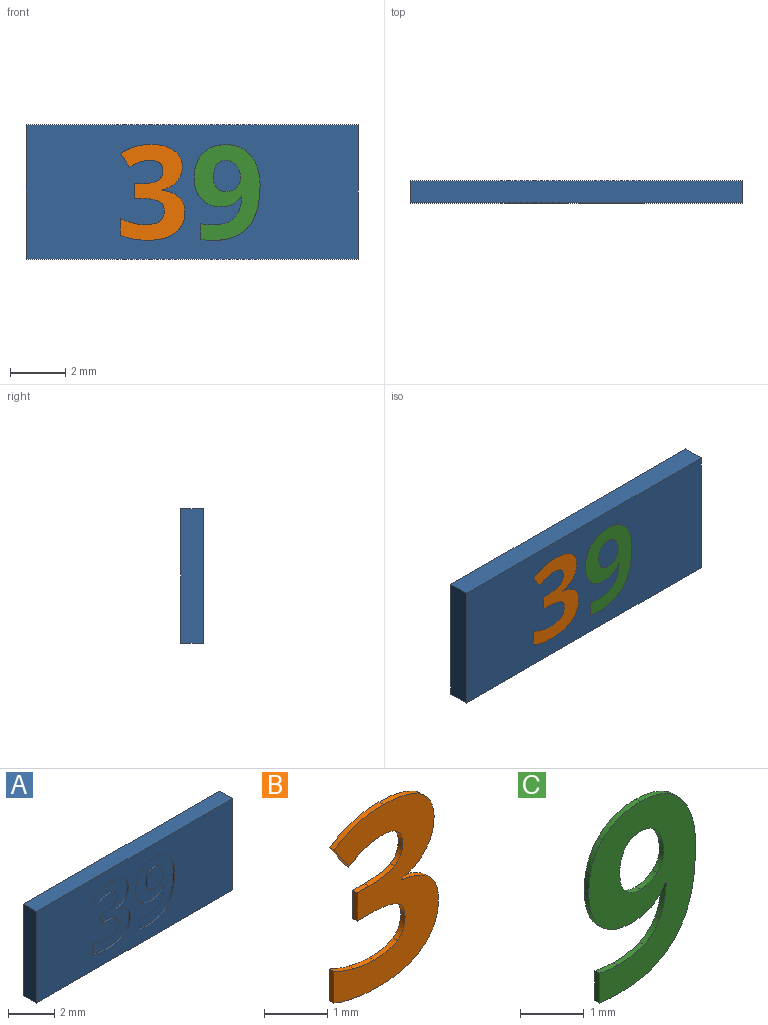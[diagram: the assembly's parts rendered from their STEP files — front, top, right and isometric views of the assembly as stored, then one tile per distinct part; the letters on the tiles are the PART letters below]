
ASSEMBLY  parts=3 mates=2
PART A: 62 faces, bbox 12x0.8x4.9 mm
  f0: plane 12x4.85mm, normal (0,-1,0), area 48.2mm2, adj f1,f2,f3,f4,f6,f7,f8,f9
  f1: plane 12x0.8mm, normal (0,0,-1), area 9.6mm2, adj f0,f2,f4,f5
  f2: plane 4.85x0.8mm, normal (1,0,0), area 3.9mm2, adj f0,f1,f3,f5
  f3: plane 12x0.8mm, normal (0,0,1), area 9.6mm2, adj f0,f2,f4,f5
  f4: plane 4.85x0.8mm, normal (-1,0,0), area 3.9mm2, adj f0,f1,f3,f5
  f5: plane 12x4.85mm, normal (0,1,0), area 58.2mm2, adj f1,f2,f3,f4
  f6: extruded ~0.79x0.15mm, area 0.1mm2, adj f0,f7,f31,f32
  f7: extruded ~0.51x0.43mm, area 0.1mm2, adj f0,f6,f8,f32
  f8: extruded ~0.65x0.18mm, area 0.1mm2, adj f0,f7,f9,f32
  f9: extruded ~0.84x0.31mm, area 0.1mm2, adj f0,f8,f10,f32
  f10: extruded ~0.86x0.31mm, area 0.1mm2, adj f0,f9,f11,f32
  f11: extruded ~0.78x0.25mm, area 0.1mm2, adj f0,f10,f12,f32
  f12: extruded ~0.69x0.28mm, area 0.1mm2, adj f0,f11,f13,f32
  f13: extruded ~0.44x0.1mm, area 0mm2, adj f0,f12,f14,f32
  f14: extruded ~0.31x0.3mm, area 0mm2, adj f0,f13,f15,f32
  f15: plane 0.1x0.03mm, normal (0,0,1), area 0mm2, adj f0,f14,f16,f32
  f16: extruded ~0.62x0.14mm, area 0.1mm2, adj f0,f15,f17,f32
  f17: extruded ~0.35x0.33mm, area 0mm2, adj f0,f16,f18,f32
  f18: extruded ~0.59x0.1mm, area 0.1mm2, adj f0,f17,f19,f32
  f19: extruded ~0.41x0.1mm, area 0mm2, adj f0,f18,f20,f32
  f20: plane 0.57x0.1mm, normal (1,0,0), area 0.1mm2, adj f0,f19,f21,f32
  f21: extruded ~0.45x0.1mm, area 0mm2, adj f0,f20,f22,f32
  f22: extruded ~1.27x0.49mm, area 0.1mm2, adj f0,f21,f31,f32
  f23: extruded ~0.37x0.19mm, area 0mm2, adj f24,f30,f32,f33
  f24: extruded ~0.46x0.14mm, area 0mm2, adj f23,f25,f32,f33
  f25: extruded ~0.33x0.15mm, area 0mm2, adj f24,f26,f32,f33
  f26: extruded ~0.37x0.14mm, area 0mm2, adj f25,f27,f32,f33
  f27: extruded ~0.34x0.14mm, area 0mm2, adj f26,f28,f32,f33
  f28: extruded ~0.39x0.11mm, area 0mm2, adj f27,f29,f32,f33
  f29: extruded ~0.44x0.12mm, area 0mm2, adj f28,f30,f32,f33
  f30: extruded ~0.35x0.15mm, area 0mm2, adj f23,f29,f32,f33
  f31: extruded ~1.49x0.42mm, area 0.2mm2, adj f0,f6,f22,f32
  f32: plane 3.46x2.38mm, normal (0,-1,0), area 4.8mm2, adj f6,f7,f8,f9,f10,f11,f12,f13
  f33: plane 1.12x0.98mm, normal (0,-1,0), area 0.9mm2, adj f23,f24,f25,f26,f27,f28,f29,f30
  f34: extruded ~0.59x0.3mm, area 0.1mm2, adj f0,f35,f60,f61
  f35: extruded ~0.83x0.21mm, area 0.1mm2, adj f0,f34,f36,f61
  f36: extruded ~1.1x0.33mm, area 0.1mm2, adj f0,f35,f37,f61
  f37: plane 0.49x0.33mm, normal (0.83,0,0.56), area 0.1mm2, adj f0,f36,f38,f61
  f38: extruded ~0.38x0.19mm, area 0mm2, adj f0,f37,f39,f61
  f39: extruded ~0.34x0.1mm, area 0mm2, adj f0,f38,f40,f61
  f40: extruded ~0.48x0.38mm, area 0.1mm2, adj f0,f39,f41,f61
  f41: extruded ~0.35x0.18mm, area 0mm2, adj f0,f40,f42,f61
  f42: extruded ~0.57x0.1mm, area 0.1mm2, adj f0,f41,f43,f61
  f43: plane 0.26x0.1mm, normal (0,0,-1), area 0mm2, adj f0,f42,f44,f61
  f44: plane 0.55x0.1mm, normal (1,0,0), area 0.1mm2, adj f0,f43,f45,f61
  f45: plane 0.26x0.1mm, normal (0,0,1), area 0mm2, adj f0,f44,f46,f61
  f46: extruded ~0.62x0.1mm, area 0.1mm2, adj f0,f45,f47,f61
  f47: extruded ~0.34x0.19mm, area 0mm2, adj f0,f46,f48,f61
  f48: extruded ~0.39x0.17mm, area 0mm2, adj f0,f47,f49,f61
  f49: extruded ~0.52x0.12mm, area 0.1mm2, adj f0,f48,f50,f61
  f50: extruded ~0.47x0.1mm, area 0mm2, adj f0,f49,f51,f61
  f51: extruded ~0.43x0.16mm, area 0mm2, adj f0,f50,f52,f61
  f52: plane 0.61x0.1mm, normal (1,0,0), area 0.1mm2, adj f0,f51,f53,f61
  f53: extruded ~0.97x0.18mm, area 0.1mm2, adj f0,f52,f54,f61
  f54: extruded ~1.01x0.27mm, area 0.1mm2, adj f0,f53,f55,f61
  f55: extruded ~0.76x0.35mm, area 0.1mm2, adj f0,f54,f56,f61
  f56: extruded ~0.53x0.21mm, area 0.1mm2, adj f0,f55,f57,f61
  f57: extruded ~0.62x0.25mm, area 0.1mm2, adj f0,f56,f58,f61
  f58: plane 0.1x0.01mm, normal (-1,0,0), area 0mm2, adj f0,f57,f59,f61
  f59: extruded ~0.54x0.3mm, area 0.1mm2, adj f0,f58,f60,f61
  f60: extruded ~0.54x0.19mm, area 0.1mm2, adj f0,f34,f59,f61
  f61: plane 3.47x2.33mm, normal (0,-1,0), area 4.3mm2, adj f34,f35,f36,f37,f38,f39,f40,f41
PART B: 29 faces, bbox 2.3x0.1x3.5 mm
  f0: plane 3.47x2.33mm, normal (0,-1,0), area 4.3mm2, adj f1,f2,f3,f4,f5,f6,f7,f8
  f1: extruded ~0.83x0.21mm, area 0.1mm2, adj f0,f2,f25,f27
  f2: extruded ~1.1x0.33mm, area 0.1mm2, adj f0,f1,f3,f25
  f3: plane 0.49x0.33mm, normal (-0.83,0,-0.56), area 0.1mm2, adj f0,f2,f4,f25
  f4: extruded ~0.38x0.19mm, area 0mm2, adj f0,f3,f5,f25
  f5: extruded ~0.34x0.1mm, area 0mm2, adj f0,f4,f6,f25
  f6: extruded ~0.48x0.38mm, area 0.1mm2, adj f0,f5,f7,f25
  f7: extruded ~0.35x0.18mm, area 0mm2, adj f0,f6,f8,f25
  f8: extruded ~0.57x0.1mm, area 0.1mm2, adj f0,f7,f9,f25
  f9: plane 0.26x0.1mm, normal (0,0,1), area 0mm2, adj f0,f8,f10,f25
  f10: plane 0.55x0.1mm, normal (-1,0,0), area 0.1mm2, adj f0,f9,f11,f25
  f11: plane 0.26x0.1mm, normal (0,0,-1), area 0mm2, adj f0,f10,f12,f25
  f12: extruded ~0.62x0.1mm, area 0.1mm2, adj f0,f11,f13,f25
  f13: extruded ~0.34x0.19mm, area 0mm2, adj f0,f12,f14,f25
  f14: extruded ~0.39x0.17mm, area 0mm2, adj f0,f13,f15,f25
  f15: extruded ~0.52x0.12mm, area 0.1mm2, adj f0,f14,f16,f25
  f16: extruded ~0.47x0.1mm, area 0mm2, adj f0,f15,f17,f25
  f17: extruded ~0.43x0.16mm, area 0mm2, adj f0,f16,f18,f25
  f18: plane 0.61x0.1mm, normal (-1,0,0), area 0.1mm2, adj f0,f17,f19,f25
  f19: extruded ~0.97x0.18mm, area 0.1mm2, adj f0,f18,f20,f25
  f20: extruded ~1.01x0.27mm, area 0.1mm2, adj f0,f19,f21,f25
  f21: extruded ~0.76x0.35mm, area 0.1mm2, adj f0,f20,f22,f25
  f22: extruded ~0.53x0.21mm, area 0.1mm2, adj f0,f21,f23,f25
  f23: extruded ~0.62x0.25mm, area 0.1mm2, adj f0,f22,f24,f25
  f24: plane 0.1x0.01mm, normal (1,0,0), area 0mm2, adj f0,f23,f25,f26
  f25: plane 3.47x2.33mm, normal (0,1,0), area 4.3mm2, adj f1,f2,f3,f4,f5,f6,f7,f8
  f26: extruded ~0.54x0.3mm, area 0.1mm2, adj f0,f24,f25,f28
  f27: extruded ~0.59x0.3mm, area 0.1mm2, adj f0,f1,f25,f28
  f28: extruded ~0.54x0.19mm, area 0.1mm2, adj f0,f25,f26,f27
PART C: 28 faces, bbox 2.4x0.1x3.5 mm
  f0: plane 3.46x2.38mm, normal (0,-1,0), area 4.8mm2, adj f1,f2,f3,f4,f5,f6,f7,f8
  f1: extruded ~0.51x0.43mm, area 0.1mm2, adj f0,f2,f21,f23
  f2: extruded ~0.65x0.18mm, area 0.1mm2, adj f0,f1,f3,f21
  f3: extruded ~0.84x0.31mm, area 0.1mm2, adj f0,f2,f4,f21
  f4: extruded ~0.86x0.31mm, area 0.1mm2, adj f0,f3,f5,f21
  f5: extruded ~0.78x0.25mm, area 0.1mm2, adj f0,f4,f6,f21
  f6: extruded ~0.69x0.28mm, area 0.1mm2, adj f0,f5,f7,f21
  f7: extruded ~0.44x0.1mm, area 0mm2, adj f0,f6,f8,f21
  f8: extruded ~0.31x0.3mm, area 0mm2, adj f0,f7,f9,f21
  f9: plane 0.1x0.03mm, normal (0,0,-1), area 0mm2, adj f0,f8,f10,f21
  f10: extruded ~0.62x0.14mm, area 0.1mm2, adj f0,f9,f11,f21
  f11: extruded ~0.35x0.33mm, area 0mm2, adj f0,f10,f12,f21
  f12: extruded ~0.59x0.1mm, area 0.1mm2, adj f0,f11,f13,f21
  f13: extruded ~0.41x0.1mm, area 0mm2, adj f0,f12,f14,f21
  f14: plane 0.57x0.1mm, normal (-1,0,0), area 0.1mm2, adj f0,f13,f15,f21
  f15: extruded ~0.45x0.1mm, area 0mm2, adj f0,f14,f21,f22
  f16: extruded ~0.46x0.14mm, area 0mm2, adj f0,f17,f21,f26
  f17: extruded ~0.33x0.15mm, area 0mm2, adj f0,f16,f18,f21
  f18: extruded ~0.37x0.14mm, area 0mm2, adj f0,f17,f19,f21
  f19: extruded ~0.34x0.14mm, area 0mm2, adj f0,f18,f20,f21
  f20: extruded ~0.39x0.11mm, area 0mm2, adj f0,f19,f21,f25
  f21: plane 3.46x2.38mm, normal (0,1,0), area 4.8mm2, adj f1,f2,f3,f4,f5,f6,f7,f8
  f22: extruded ~1.27x0.49mm, area 0.1mm2, adj f0,f15,f21,f24
  f23: extruded ~0.79x0.15mm, area 0.1mm2, adj f0,f1,f21,f24
  f24: extruded ~1.49x0.42mm, area 0.2mm2, adj f0,f21,f22,f23
  f25: extruded ~0.44x0.12mm, area 0mm2, adj f0,f20,f21,f27
  f26: extruded ~0.37x0.19mm, area 0mm2, adj f0,f16,f21,f27
  f27: extruded ~0.35x0.15mm, area 0mm2, adj f0,f21,f25,f26
PLACE A t=(0.02,0.42,0.02)mm
PLACE B t=(-2.9,0.42,0.02)mm
PLACE C t=(-0.2,0.42,0.02)mm
MATE fastened C.f0 <-> A.f0  axis (0,-1,0) through (0.34,-0.38,-1.7)mm
MATE fastened B.f0 <-> A.f0  axis (0,-1,0) through (-2.57,-0.38,-1.55)mm
